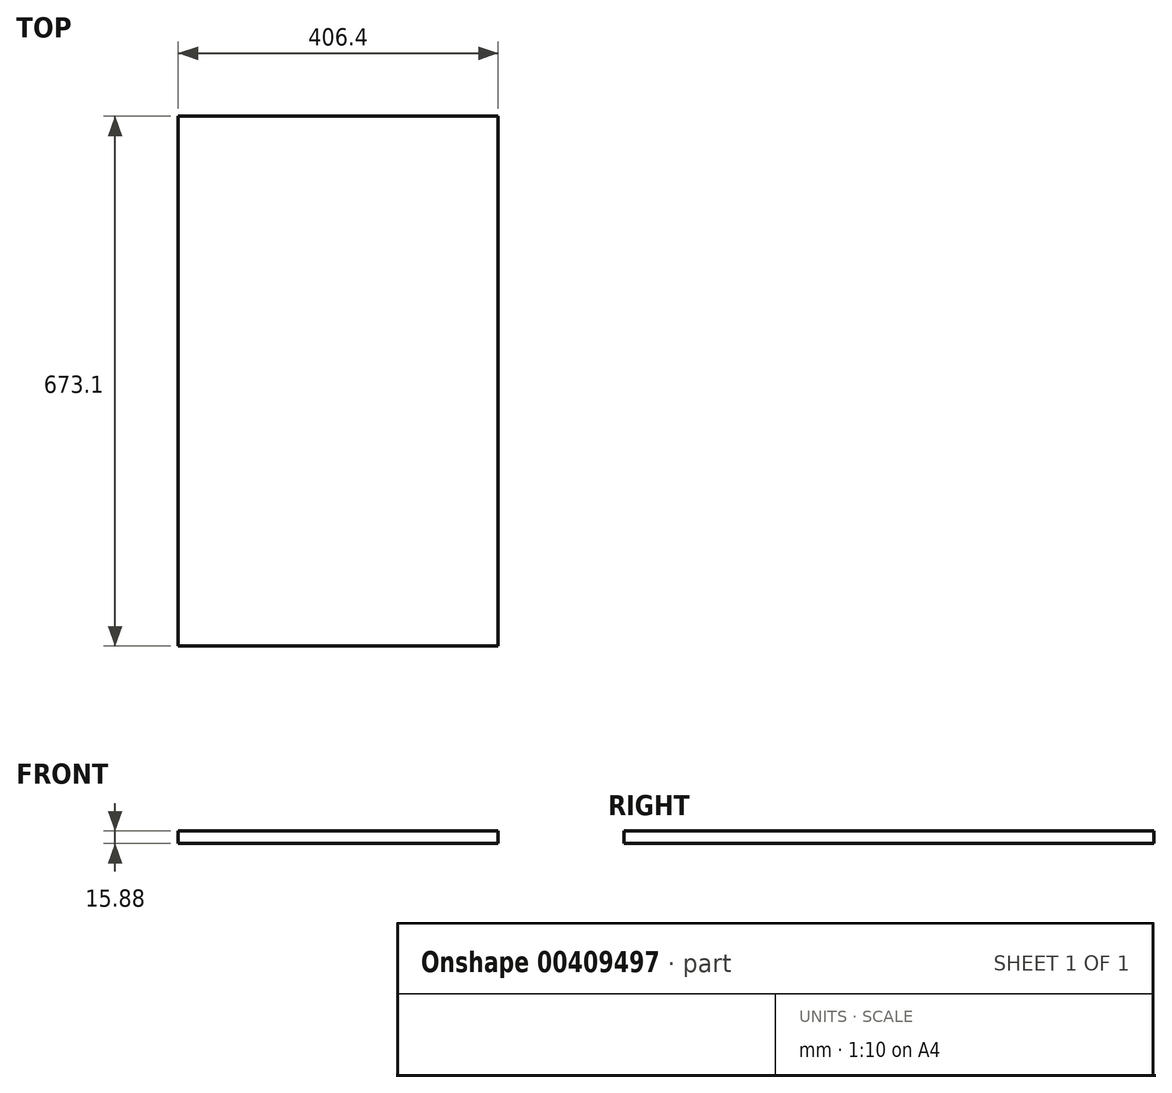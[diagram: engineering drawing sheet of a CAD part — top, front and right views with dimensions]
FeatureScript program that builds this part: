
annotation { "Feature Type Name" : "Feature", "Feature Type Description" : "" }
export const myFeature = defineFeature(function(context is Context, id is Id, definition is map)
    precondition{}
    {
        {
            var Q0;
            Q0=qCreatedBy(makeId("Front.planeOp"),FACE);
            var sketch = newSketch(context, id + "F0", { "sketchPlane" : qUnion([Q0])});
            skLineSegment(sketch, "E0.bottom", {"start": v(0, 0) * mm, "end": v(406.4, 0) * mm});
            skLineSegment(sketch, "E0.top", {"start": v(0, 15.87) * mm, "end": v(406.4, 15.87) * mm});
            skLineSegment(sketch, "E0.left", {"start": v(0, 0) * mm, "end": v(0, 15.87) * mm});
            skLineSegment(sketch, "E0.right", {"start": v(406.4, 0) * mm, "end": v(406.4, 15.87) * mm});
            skSolve(sketch);
        }
        {
            var Q0;
            Q0=makeQuery(id+"F0.imprint","IMPRINT",FACE,{"disambiguationData":[TD([[makeQuery(id+"F0.imprint","IMPRINT",EDGE,{"derivedFrom":sQuery(id+"F0.wireOp",EDGE,"E0.bottom")}),1.0]])]});
            extrude(context, id + "F1", {"entities" : qUnion([Q0]), "depth" : 673.1 * mm});
        }
    });
